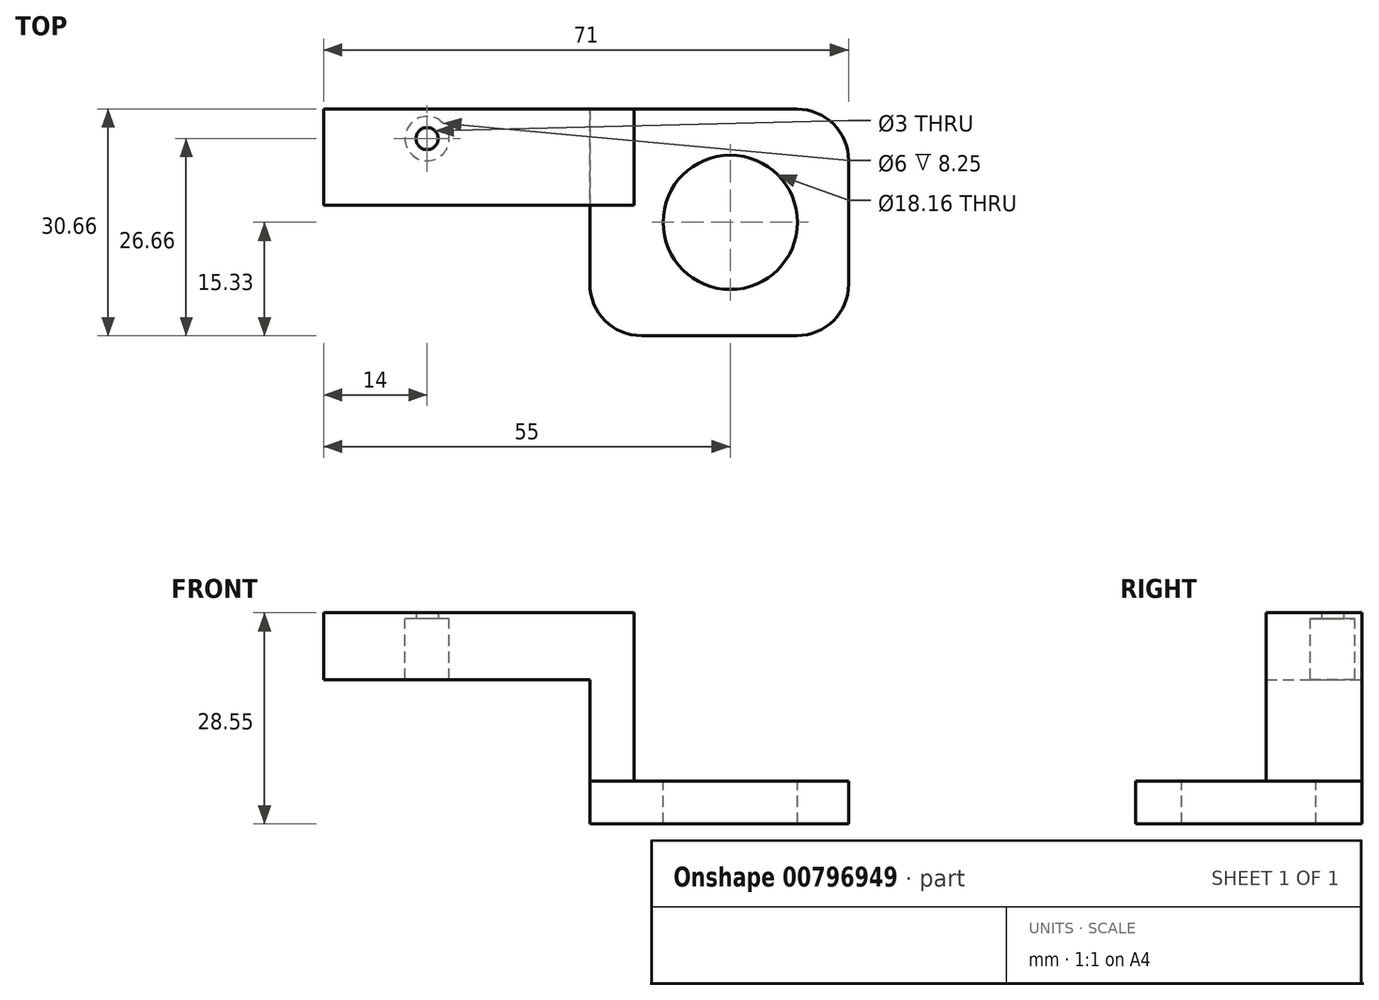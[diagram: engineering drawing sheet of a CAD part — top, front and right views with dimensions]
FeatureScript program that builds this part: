
annotation { "Feature Type Name" : "Feature", "Feature Type Description" : "" }
export const myFeature = defineFeature(function(context is Context, id is Id, definition is map)
    precondition{}
    {
        {
            var Q0;
            Q0=qCreatedBy(makeId("Top.planeOp"),FACE);
            var sketch = newSketch(context, id + "F0", { "sketchPlane" : qUnion([Q0])});
            skLineSegment(sketch, "E0.bottom", {"start": v(0, 0) * mm, "end": v(-42, 0) * mm});
            skLineSegment(sketch, "E0.top", {"start": v(0, 13) * mm, "end": v(-42, 13) * mm});
            skLineSegment(sketch, "E0.left", {"start": v(0, 0) * mm, "end": v(0, 13) * mm});
            skLineSegment(sketch, "E0.right", {"start": v(-42, 0) * mm, "end": v(-42, 13) * mm});
            skCircle(sketch, "E1", {"center": v(-28, 9) * mm, "radius": 3 * mm});
            skCircle(sketch, "E2", {"center": v(-28, 9) * mm, "radius": 1.5 * mm});
            skLineSegment(sketch, "E3.bottom", {"start": v(0, 13) * mm, "end": v(-6, 13) * mm});
            skLineSegment(sketch, "E3.top", {"start": v(0, 0) * mm, "end": v(-6, 0) * mm});
            skLineSegment(sketch, "E3.left", {"start": v(0, 13) * mm, "end": v(0, 0) * mm});
            skLineSegment(sketch, "E3.right", {"start": v(-6, 13) * mm, "end": v(-6, 0) * mm});
            skSolve(sketch);
        }
        {
            var Q0;
            {var subQ2=sQuery(id+"F0.wireOp",EDGE,"E0.left");Q0=makeQuery(id+"F0.imprint","IMPRINT",FACE,{"disambiguationData":[TD([[makeQuery(id+"F0.imprint","IMPRINT",EDGE,{"derivedFrom":subQ2}),1.0]])]});}
            var Q1;
            {var subQ2=sQuery(id+"F0.wireOp",EDGE,"E0.right");Q1=makeQuery(id+"F0.imprint","IMPRINT",FACE,{"disambiguationData":[TD([[makeQuery(id+"F0.imprint","IMPRINT",EDGE,{"derivedFrom":subQ2}),-1.0]])]});}
            var Q2;
            Q2=makeQuery(id+"F0.imprint","IMPRINT",FACE,{"disambiguationData":[TD([[makeQuery(id+"F0.imprint","IMPRINT",EDGE,{"derivedFrom":sQuery(id+"F0.wireOp",EDGE,"E1")}),1.0]])]});
            extrude(context, id + "F1", {"entities" : qUnion([Q0, Q1, Q2]), "depth" : 0.8 * mm, "offsetDistance" : 25 * mm});
        }
        {
            var Q0;
            {var subQ2=sQuery(id+"F0.wireOp",EDGE,"E0.left");Q0=makeQuery(id+"F0.imprint","IMPRINT",FACE,{"disambiguationData":[TD([[makeQuery(id+"F0.imprint","IMPRINT",EDGE,{"derivedFrom":subQ2}),1.0]])]});}
            extrude(context, id + "F2", {"entities" : qUnion([Q0]), "operationType" : NewBodyOperationType.ADD, "oppositeDirection" : true, "depth" : 22 * mm, "offsetDistance" : 25 * mm});
        }
        {
            var Q0;
            {var subQ2=sQuery(id+"F0.wireOp",EDGE,"E0.right");Q0=makeQuery(id+"F0.imprint","IMPRINT",FACE,{"disambiguationData":[TD([[makeQuery(id+"F0.imprint","IMPRINT",EDGE,{"derivedFrom":subQ2}),-1.0]])]});}
            extrude(context, id + "F3", {"entities" : qUnion([Q0]), "operationType" : NewBodyOperationType.ADD, "depth" : -8.25 * mm, "offsetDistance" : 25 * mm});
        }
        {
            var Q0;
            Q0=makeQuery(id+"F2.opExtrude","CAP_FACE",FACE,{"disambiguationData":[OSD([sQuery(id+"F0.wireOp",EDGE,"E0.bottom"),sQuery(id+"F0.wireOp",EDGE,"E0.top"),sQuery(id+"F0.wireOp",EDGE,"E0.left"),sQuery(id+"F0.wireOp",EDGE,"E3.right")])],"isStart":false});
            var sketch = newSketch(context, id + "F4", { "sketchPlane" : qUnion([Q0])});
            skLineSegment(sketch, "E4.bottom", {"start": v(-6, 17.66) * mm, "end": v(29, 17.66) * mm});
            skLineSegment(sketch, "E4.top", {"start": v(-6, -13) * mm, "end": v(29, -13) * mm});
            skLineSegment(sketch, "E4.left", {"start": v(-6, 17.66) * mm, "end": v(-6, -13) * mm});
            skLineSegment(sketch, "E4.right", {"start": v(29, 17.66) * mm, "end": v(29, -13) * mm});
            skCircle(sketch, "E5", {"center": v(13, 2.33) * mm, "radius": 9.08 * mm});
            skLineSegment(sketch, "E6", {"start": v(0, -13) * mm, "end": v(17.6, -13) * mm});
            skCircle(sketch, "E7", {"center": v(13, 2.33) * mm, "radius": 13 * mm});
            skSolve(sketch);
        }
        {
            var Q0;
            {var subQ4=sQuery(id+"F4.wireOp",EDGE,"E4.bottom");Q0=makeQuery(id+"F4.imprint","IMPRINT",FACE,{"disambiguationData":[TD([[makeQuery(id+"F4.imprint","IMPRINT",EDGE,{"derivedFrom":subQ4}),-1.0]])]});}
            var Q1;
            {var subQ1=makeQuery(id+"F2.opExtrude","CAP_EDGE",EDGE,{"disambiguationData":[OSD([sQuery(id+"F0.wireOp",EDGE,"E3.bottom")])],"isStart":false});Q1=makeQuery(id+"F4.imprint","IMPRINT",FACE,{"disambiguationData":[TD([[makeQuery(id+"F4.imprint","IMPRINT",EDGE,{"derivedFrom":subQ1}),-1.0]])]});}
            var Q2;
            {var subQ0=sQuery(id+"F4.wireOp",EDGE,"E6");var subQ3=sQuery(id+"F4.wireOp",EDGE,"E7");var subQ4=makeQuery(id+"F4.imprint","INTERSECT",VERTEX,{"derivedFrom":[subQ0,subQ3]});Q2=makeQuery(id+"F4.imprint","IMPRINT",FACE,{"disambiguationData":[TD([[makeQuery(id+"F4.imprint","IMPRINT",EDGE,{"disambiguationData":[TD([[subQ4,1.0]])],"derivedFrom":subQ3}),-1.0]])]});}
            var Q3;
            Q3=makeQuery(id+"F4.imprint","IMPRINT",FACE,{"disambiguationData":[TD([[makeQuery(id+"F4.imprint","IMPRINT",EDGE,{"derivedFrom":sQuery(id+"F4.wireOp",EDGE,"E5")}),-1.0]])]});
            var Q4;
            {var subQ4=makeQuery(id+"F2.opExtrude","CAP_EDGE",EDGE,{"disambiguationData":[OSD([sQuery(id+"F0.wireOp",EDGE,"E0.bottom")])],"isStart":false});Q4=makeQuery(id+"F4.imprint","IMPRINT",FACE,{"disambiguationData":[TD([[makeQuery(id+"F4.imprint","IMPRINT",EDGE,{"derivedFrom":subQ4}),1.0]])]});}
            extrude(context, id + "F5", {"entities" : qUnion([Q0, Q1, Q2, Q3, Q4]), "operationType" : NewBodyOperationType.ADD, "depth" : 5.75 * mm, "offsetDistance" : 25 * mm});
        }
        {
            var Q0;
            Q0=makeQuery(id+"F5.opExtrude","SWEPT_EDGE",EDGE,{"disambiguationData":[OSD([sQuery(id+"F4.wireOp",EDGE,"E4.bottom"),sQuery(id+"F4.wireOp",EDGE,"E4.left")])]});
            var Q1;
            Q1=makeQuery(id+"F5.opExtrude","SWEPT_EDGE",EDGE,{"disambiguationData":[OSD([sQuery(id+"F4.wireOp",EDGE,"E4.bottom"),sQuery(id+"F4.wireOp",EDGE,"E4.right")])]});
            var Q2;
            Q2=makeQuery(id+"F5.opExtrude","SWEPT_EDGE",EDGE,{"disambiguationData":[OSD([sQuery(id+"F4.wireOp",EDGE,"E4.top"),sQuery(id+"F4.wireOp",EDGE,"E4.right")])]});
            fillet(context, id + "F6", {"entities" : qUnion([Q0, Q1, Q2]), "radius" : 7 * mm, "tangentPropagation" : true, "allowEdgeOverflow" : false});
        }
    });
